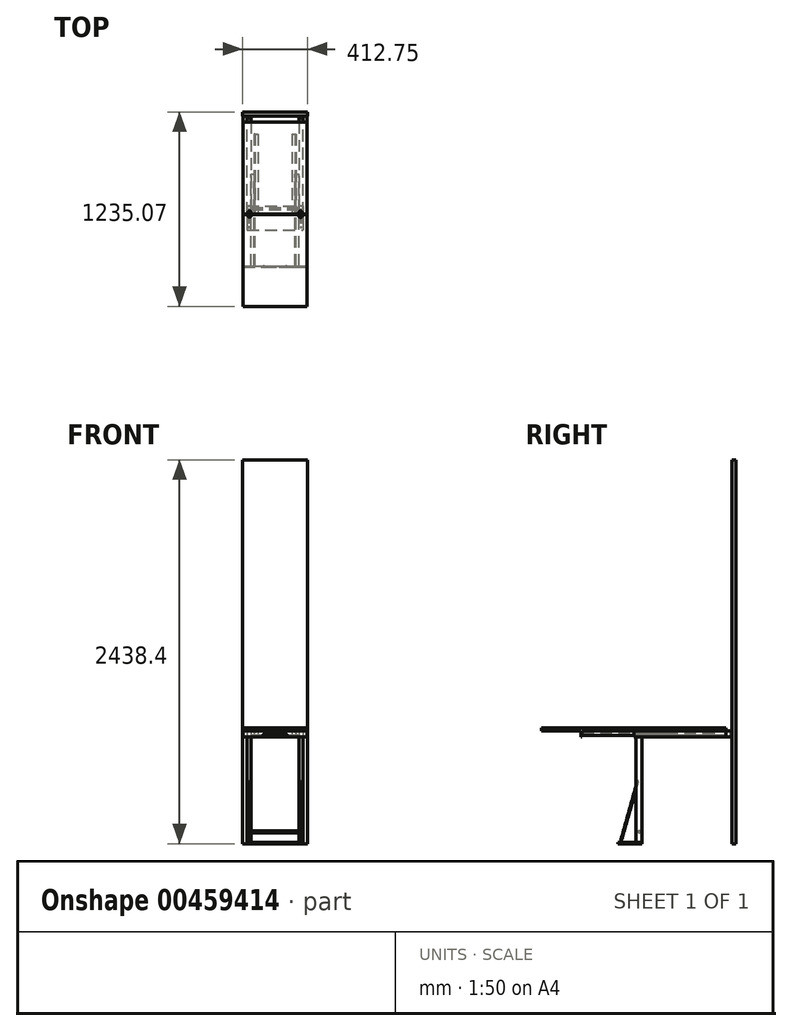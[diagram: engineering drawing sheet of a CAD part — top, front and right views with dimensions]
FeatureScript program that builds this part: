
annotation { "Feature Type Name" : "Feature", "Feature Type Description" : "" }
export const myFeature = defineFeature(function(context is Context, id is Id, definition is map)
    precondition{}
    {
        {
            var Q0;
            Q0=qCreatedBy(makeId("Front.planeOp"),FACE);
            var sketch = newSketch(context, id + "F0", { "sketchPlane" : qUnion([Q0])});
            skLineSegment(sketch, "E0.bottom", {"start": v(0, 0) * mm, "end": v(412.75, 0) * mm});
            skLineSegment(sketch, "E0.top", {"start": v(0, 2438.4) * mm, "end": v(412.75, 2438.4) * mm});
            skLineSegment(sketch, "E0.left", {"start": v(0, 0) * mm, "end": v(0, 2438.4) * mm});
            skLineSegment(sketch, "E0.right", {"start": v(412.75, 0) * mm, "end": v(412.75, 2438.4) * mm});
            skSolve(sketch);
        }
        {
            var Q0;
            Q0=qSketchRegion(id+"F0",true);
            extrude(context, id + "F1", {"entities" : qUnion([Q0]), "depth" : 25.4 * mm});
        }
        {
            var Q0;
            Q0=makeQuery(id+"F1.opExtrude","CAP_FACE",FACE,{"disambiguationData":[OSD([sQuery(id+"F0.wireOp",EDGE,"E0.bottom"),sQuery(id+"F0.wireOp",EDGE,"E0.top"),sQuery(id+"F0.wireOp",EDGE,"E0.left"),sQuery(id+"F0.wireOp",EDGE,"E0.right")])],"isStart":false});
            var sketch = newSketch(context, id + "F2", { "sketchPlane" : qUnion([Q0])});
            skLineSegment(sketch, "E1", {"start": v(206.38, 0) * mm, "end": v(206.38, 1295.4) * mm, "construction": true});
            skPoint(sketch, "E2", {"position": v(206.38, 736.6) * mm});
            skSolve(sketch);
        }
        {
            var Q0;
            Q0=makeQuery(id+"F2.imprint","IMPRINT",FACE,{"disambiguationData":[TD([[makeQuery(id+"F2.imprint","IMPRINT",EDGE,{"derivedFrom":makeQuery(id+"F1.opExtrude","CAP_EDGE",EDGE,{"disambiguationData":[OSD([sQuery(id+"F0.wireOp",EDGE,"E0.bottom")])],"isStart":false})}),1.0]])]});
            var sketch = newSketch(context, id + "F3", { "sketchPlane" : qUnion([Q0])});
            skLineSegment(sketch, "E3.bottom", {"start": v(3.17, 717.55) * mm, "end": v(409.58, 717.55) * mm});
            skLineSegment(sketch, "E3.top", {"start": v(3.18, 679.45) * mm, "end": v(409.57, 679.45) * mm});
            skLineSegment(sketch, "E3.left", {"start": v(3.17, 717.55) * mm, "end": v(3.17, 679.45) * mm});
            skLineSegment(sketch, "E3.right", {"start": v(409.57, 717.55) * mm, "end": v(409.57, 679.45) * mm});
            skLineSegment(sketch, "E4", {"start": v(206.37, 717.55) * mm, "end": v(206.37, 764.95) * mm, "construction": true});
            skSolve(sketch);
        }
        {
            var Q0;
            Q0 = qSketchRegion(id + "F3", true);
            extrude(context, id + "F4", {"entities" : qUnion([Q0]), "depth" : 38.1 * mm});
        }
        {
            var Q0;
            Q0=makeQuery(id+"F4.opExtrude","SWEPT_FACE",FACE,{"disambiguationData":[OSD([sQuery(id+"F3.wireOp",EDGE,"E3.bottom")])]});
            var sketch = newSketch(context, id + "F5", { "sketchPlane" : qUnion([Q0])});
            skLineSegment(sketch, "E5.bottom", {"start": v(3.17, -25.4) * mm, "end": v(409.58, -25.4) * mm});
            skLineSegment(sketch, "E5.top", {"start": v(3.17, -43.66) * mm, "end": v(409.58, -43.66) * mm});
            skLineSegment(sketch, "E5.left", {"start": v(3.17, -25.4) * mm, "end": v(3.17, -43.66) * mm});
            skLineSegment(sketch, "E5.right", {"start": v(409.58, -25.4) * mm, "end": v(409.58, -43.66) * mm});
            skLineSegment(sketch, "E6.bottom", {"start": v(3.17, -63.5) * mm, "end": v(409.58, -63.5) * mm});
            skLineSegment(sketch, "E6.top", {"start": v(3.17, -45.24) * mm, "end": v(409.58, -45.24) * mm});
            skLineSegment(sketch, "E6.left", {"start": v(3.17, -63.5) * mm, "end": v(3.17, -45.24) * mm});
            skLineSegment(sketch, "E6.right", {"start": v(409.58, -63.5) * mm, "end": v(409.58, -45.24) * mm});
            skSolve(sketch);
        }
        {
            var Q0;
            Q0 = qSketchRegion(id + "F5", true);
            var Q1;
            Q1=sQuery(id+"F2.wireOp",VERTEX,"E1.end");
            extrude(context, id + "F6", {"entities" : qUnion([Q0]), "endBound" : BoundingType.UP_TO_VERTEX, "endBoundEntityVertex" : qUnion([Q1]), "depth" : 25.4 * mm});
        }
        {
            var Q0;
            Q0=makeQuery(id+"F4.opExtrude","CAP_FACE",FACE,{"disambiguationData":[OSD([sQuery(id+"F3.wireOp",EDGE,"E3.bottom"),sQuery(id+"F3.wireOp",EDGE,"E3.top"),sQuery(id+"F3.wireOp",EDGE,"E3.left"),sQuery(id+"F3.wireOp",EDGE,"E3.right")])],"isStart":false});
            var sketch = newSketch(context, id + "F7", { "sketchPlane" : qUnion([Q0])});
            skLineSegment(sketch, "E7.bottom", {"start": v(3.17, 717.55) * mm, "end": v(28.57, 717.55) * mm});
            skLineSegment(sketch, "E7.top", {"start": v(3.17, 679.45) * mm, "end": v(28.57, 679.45) * mm});
            skLineSegment(sketch, "E7.left", {"start": v(3.17, 717.55) * mm, "end": v(3.17, 679.45) * mm});
            skLineSegment(sketch, "E7.right", {"start": v(28.57, 717.55) * mm, "end": v(28.57, 679.45) * mm});
            skLineSegment(sketch, "E8.bottom", {"start": v(409.57, 679.45) * mm, "end": v(384.17, 679.45) * mm});
            skLineSegment(sketch, "E8.top", {"start": v(409.57, 717.55) * mm, "end": v(384.17, 717.55) * mm});
            skLineSegment(sketch, "E8.left", {"start": v(409.57, 679.45) * mm, "end": v(409.57, 717.55) * mm});
            skLineSegment(sketch, "E8.right", {"start": v(384.17, 679.45) * mm, "end": v(384.17, 717.55) * mm});
            skSolve(sketch);
        }
        {
            var Q0;
            Q0 = qSketchRegion(id + "F7", true);
            extrude(context, id + "F8", {"entities" : qUnion([Q0]), "depth" : 584.2 * mm});
        }
        {
            var Q0;
            Q0=makeQuery(id+"F8.opExtrude","CAP_FACE",FACE,{"disambiguationData":[OSD([sQuery(id+"F7.wireOp",EDGE,"E8.bottom"),sQuery(id+"F7.wireOp",EDGE,"E8.top"),sQuery(id+"F7.wireOp",EDGE,"E8.left"),sQuery(id+"F7.wireOp",EDGE,"E8.right")])],"isStart":false});
            var sketch = newSketch(context, id + "F9", { "sketchPlane" : qUnion([Q0])});
            skLineSegment(sketch, "E9.bottom", {"start": v(53.97, 717.55) * mm, "end": v(79.37, 717.55) * mm});
            skLineSegment(sketch, "E9.top", {"start": v(53.97, 679.45) * mm, "end": v(79.37, 679.45) * mm});
            skLineSegment(sketch, "E9.left", {"start": v(53.97, 717.55) * mm, "end": v(53.97, 679.45) * mm});
            skLineSegment(sketch, "E9.right", {"start": v(79.37, 717.55) * mm, "end": v(79.37, 704.85) * mm});
            skLineSegment(sketch, "E10.bottom", {"start": v(333.38, 717.55) * mm, "end": v(358.78, 717.55) * mm});
            skLineSegment(sketch, "E10.top", {"start": v(333.38, 679.45) * mm, "end": v(358.78, 679.45) * mm});
            skLineSegment(sketch, "E10.left", {"start": v(333.38, 717.55) * mm, "end": v(333.38, 704.85) * mm});
            skLineSegment(sketch, "E10.right", {"start": v(358.78, 717.55) * mm, "end": v(358.78, 679.45) * mm});
            skLineSegment(sketch, "E11", {"start": v(53.97, 698.5) * mm, "end": v(358.78, 698.5) * mm, "construction": true});
            skLineSegment(sketch, "E12", {"start": v(358.78, 698.5) * mm, "end": v(206.37, 698.5) * mm, "construction": true});
            skLineSegment(sketch, "E13", {"start": v(206.37, 698.5) * mm, "end": v(206.37, 1295.4) * mm, "construction": true});
            skLineSegment(sketch, "E14.bottom", {"start": v(79.37, 704.85) * mm, "end": v(73.02, 704.85) * mm});
            skLineSegment(sketch, "E14.top", {"start": v(79.37, 692.15) * mm, "end": v(73.02, 692.15) * mm});
            skLineSegment(sketch, "E14.right", {"start": v(73.02, 704.85) * mm, "end": v(73.02, 692.15) * mm});
            skLineSegment(sketch, "E15.bottom", {"start": v(333.38, 704.85) * mm, "end": v(339.73, 704.85) * mm});
            skLineSegment(sketch, "E15.top", {"start": v(333.38, 692.15) * mm, "end": v(339.73, 692.15) * mm});
            skLineSegment(sketch, "E15.right", {"start": v(339.73, 704.85) * mm, "end": v(339.73, 692.15) * mm});
            skLineSegment(sketch, "E16", {"start": v(73.02, 698.5) * mm, "end": v(91.35, 698.5) * mm, "construction": true});
            skLineSegment(sketch, "E17.trimOffspring", {"start": v(79.37, 692.15) * mm, "end": v(79.37, 679.45) * mm});
            skLineSegment(sketch, "E18.trimOffspring", {"start": v(333.38, 692.15) * mm, "end": v(333.38, 679.45) * mm});
            skSolve(sketch);
        }
        {
            var Q0;
            Q0 = qSketchRegion(id + "F9", true);
            extrude(context, id + "F10", {"entities" : qUnion([Q0]), "depth" : 330.2 * mm, "hasSecondDirection" : true, "secondDirectionOppositeDirection" : true, "secondDirectionDepth" : 254 * mm});
        }
        {
            var Q0;
            Q0=makeQuery(id+"F10.opExtrude","CAP_FACE",FACE,{"disambiguationData":[OSD([sQuery(id+"F9.wireOp",EDGE,"E9.bottom"),sQuery(id+"F9.wireOp",EDGE,"E9.top"),sQuery(id+"F9.wireOp",EDGE,"E9.left"),sQuery(id+"F9.wireOp",EDGE,"E9.right"),sQuery(id+"F9.wireOp",EDGE,"E14.bottom"),sQuery(id+"F9.wireOp",EDGE,"E14.top"),sQuery(id+"F9.wireOp",EDGE,"E14.right"),sQuery(id+"F9.wireOp",EDGE,"E17.trimOffspring")])],"isStart":false});
            var sketch = newSketch(context, id + "F11", { "sketchPlane" : qUnion([Q0])});
            skLineSegment(sketch, "E19.bottom", {"start": v(53.97, 679.45) * mm, "end": v(358.78, 679.45) * mm});
            skLineSegment(sketch, "E19.top", {"start": v(53.97, 717.55) * mm, "end": v(358.78, 717.55) * mm});
            skLineSegment(sketch, "E19.left", {"start": v(53.97, 679.45) * mm, "end": v(53.97, 717.55) * mm});
            skLineSegment(sketch, "E19.right", {"start": v(358.78, 679.45) * mm, "end": v(358.78, 717.55) * mm});
            skSolve(sketch);
        }
        {
            var Q0;
            Q0 = qSketchRegion(id + "F11", true);
            extrude(context, id + "F12", {"entities" : qUnion([Q0]), "depth" : 6.35 * mm});
        }
        {
            var Q0;
            Q0=makeQuery(id+"F8.opExtrude","CAP_FACE",FACE,{"disambiguationData":[OSD([sQuery(id+"F7.wireOp",EDGE,"E7.bottom"),sQuery(id+"F7.wireOp",EDGE,"E7.top"),sQuery(id+"F7.wireOp",EDGE,"E7.left"),sQuery(id+"F7.wireOp",EDGE,"E7.right")])],"isStart":false});
            var sketch = newSketch(context, id + "F13", { "sketchPlane" : qUnion([Q0])});
            skLineSegment(sketch, "E20.0", {"start": v(79.37, 717.55) * mm, "end": v(79.37, 704.85) * mm});
            skLineSegment(sketch, "E20.1", {"start": v(79.37, 704.85) * mm, "end": v(73.02, 704.85) * mm});
            skLineSegment(sketch, "E20.2", {"start": v(73.02, 704.85) * mm, "end": v(73.02, 692.15) * mm});
            skLineSegment(sketch, "E20.3", {"start": v(79.37, 692.15) * mm, "end": v(73.02, 692.15) * mm});
            skLineSegment(sketch, "E20.4", {"start": v(79.37, 692.15) * mm, "end": v(79.37, 679.45) * mm});
            skLineSegment(sketch, "E20.5", {"start": v(333.38, 717.55) * mm, "end": v(333.38, 704.85) * mm});
            skLineSegment(sketch, "E20.6", {"start": v(333.38, 704.85) * mm, "end": v(339.73, 704.85) * mm});
            skLineSegment(sketch, "E20.7", {"start": v(339.73, 704.85) * mm, "end": v(339.73, 692.15) * mm});
            skLineSegment(sketch, "E20.8", {"start": v(333.38, 692.15) * mm, "end": v(339.73, 692.15) * mm});
            skLineSegment(sketch, "E20.9", {"start": v(333.38, 692.15) * mm, "end": v(333.38, 679.45) * mm});
            skLineSegment(sketch, "E21", {"start": v(333.38, 717.55) * mm, "end": v(314.33, 717.55) * mm});
            skLineSegment(sketch, "E22", {"start": v(314.33, 717.55) * mm, "end": v(314.33, 679.45) * mm});
            skLineSegment(sketch, "E23", {"start": v(314.33, 679.45) * mm, "end": v(333.38, 679.45) * mm});
            skLineSegment(sketch, "E24", {"start": v(79.37, 717.55) * mm, "end": v(98.42, 717.55) * mm});
            skLineSegment(sketch, "E25", {"start": v(98.42, 717.55) * mm, "end": v(98.42, 679.45) * mm});
            skLineSegment(sketch, "E26", {"start": v(98.42, 679.45) * mm, "end": v(79.37, 679.45) * mm});
            skSolve(sketch);
        }
        {
            var Q0;
            Q0 = qSketchRegion(id + "F13", true);
            extrude(context, id + "F14", {"entities" : qUnion([Q0]), "oppositeDirection" : true, "depth" : 508 * mm});
        }
        {
            var Q0;
            Q0=makeQuery(id+"F14.opExtrude","SWEPT_FACE",FACE,{"disambiguationData":[OSD([sQuery(id+"F13.wireOp",EDGE,"E23")])]});
            var sketch = newSketch(context, id + "F15", { "sketchPlane" : qUnion([Q0])});
            skLineSegment(sketch, "E27.bottom", {"start": v(44.15, 977.9) * mm, "end": v(373.47, 977.9) * mm});
            skLineSegment(sketch, "E27.top", {"start": v(44.15, 63.5) * mm, "end": v(373.47, 63.5) * mm});
            skLineSegment(sketch, "E27.left", {"start": v(44.15, 977.9) * mm, "end": v(44.15, 63.5) * mm});
            skLineSegment(sketch, "E27.right", {"start": v(373.47, 977.9) * mm, "end": v(373.47, 63.5) * mm});
            skSolve(sketch);
        }
        {
            var Q0;
            Q0 = qSketchRegion(id + "F15", true);
            extrude(context, id + "F16", {"entities" : qUnion([Q0]), "operationType" : NewBodyOperationType.REMOVE, "oppositeDirection" : true, "depth" : 9.52 * mm});
        }
        {
            var Q0;
            Q0=makeQuery(id+"F8.opExtrude","SWEPT_FACE",FACE,{"disambiguationData":[OSD([sQuery(id+"F7.wireOp",EDGE,"E8.bottom")])]});
            var sketch = newSketch(context, id + "F17", { "sketchPlane" : qUnion([Q0])});
            skLineSegment(sketch, "E28.bottom", {"start": v(53.97, 647.7) * mm, "end": v(358.78, 647.7) * mm});
            skLineSegment(sketch, "E28.top", {"start": v(53.97, 63.5) * mm, "end": v(358.78, 63.5) * mm});
            skLineSegment(sketch, "E28.left", {"start": v(53.97, 647.7) * mm, "end": v(53.97, 63.5) * mm});
            skLineSegment(sketch, "E28.right", {"start": v(358.78, 647.7) * mm, "end": v(358.78, 63.5) * mm});
            skSolve(sketch);
        }
        {
            var Q0;
            Q0 = qSketchRegion(id + "F17", true);
            var Q1;
            {var subQ5=sQuery(id+"F9.wireOp",EDGE,"E9.left");Q1=makeQuery(id+"F16.boolean.opBoolean","COPY",FACE,{"disambiguationData":[TD([makeQuery(id+"F10.opExtrude","SWEPT_FACE",FACE,{"disambiguationData":[OSD([subQ5])]})])],"derivedFrom":makeQuery(id+"F16.opExtrude","CAP_FACE",FACE,{"disambiguationData":[OSD([sQuery(id+"F15.wireOp",EDGE,"E27.bottom"),sQuery(id+"F15.wireOp",EDGE,"E27.top"),sQuery(id+"F15.wireOp",EDGE,"E27.left"),sQuery(id+"F15.wireOp",EDGE,"E27.right")])],"isStart":false})});}
            extrude(context, id + "F18", {"entities" : qUnion([Q0]), "endBound" : BoundingType.UP_TO_SURFACE, "oppositeDirection" : true, "endBoundEntityFace" : qUnion([Q1]), "depth" : 25.4 * mm});
        }
        {
            var Q0;
            Q0=makeQuery(id+"F12.opExtrude","CAP_FACE",FACE,{"disambiguationData":[OSD([sQuery(id+"F11.wireOp",EDGE,"E19.bottom"),sQuery(id+"F11.wireOp",EDGE,"E19.top"),sQuery(id+"F11.wireOp",EDGE,"E19.left"),sQuery(id+"F11.wireOp",EDGE,"E19.right")])],"isStart":false});
            var sketch = newSketch(context, id + "F19", { "sketchPlane" : qUnion([Q0])});
            skLineSegment(sketch, "E29.top", {"start": v(139.7, 698.5) * mm, "end": v(273.05, 698.5) * mm});
            skLineSegment(sketch, "E29.left", {"start": v(130.17, 685.8) * mm, "end": v(130.17, 688.98) * mm});
            skLineSegment(sketch, "E29.right", {"start": v(282.57, 685.8) * mm, "end": v(282.57, 688.98) * mm});
            skLineSegment(sketch, "E30", {"start": v(206.37, 698.5) * mm, "end": v(206.37, 717.55) * mm, "construction": true});
            skPoint(sketch, "E31.visualSharp", {"position": v(130.17, 698.5) * mm});
            skArc(sketch, "E31.filletArc", {"start": v(139.7, 698.5) * mm, "mid": v(132.96, 695.71) * mm, "end": v(130.17, 688.98) * mm});
            skPoint(sketch, "E32.visualSharp", {"position": v(282.58, 698.5) * mm});
            skArc(sketch, "E32.filletArc", {"start": v(282.57, 688.98) * mm, "mid": v(279.79, 695.71) * mm, "end": v(273.05, 698.5) * mm});
            skLineSegment(sketch, "E33", {"start": v(123.82, 679.45) * mm, "end": v(104.54, 679.45) * mm});
            skLineSegment(sketch, "E34", {"start": v(104.54, 679.45) * mm, "end": v(95.15, 663.43) * mm});
            skLineSegment(sketch, "E35", {"start": v(95.15, 663.43) * mm, "end": v(306.09, 663.43) * mm});
            skLineSegment(sketch, "E36", {"start": v(306.09, 663.43) * mm, "end": v(306.09, 679.45) * mm});
            skLineSegment(sketch, "E37", {"start": v(306.09, 679.45) * mm, "end": v(288.92, 679.45) * mm});
            skPoint(sketch, "E38.visualSharp", {"position": v(130.17, 679.45) * mm});
            skArc(sketch, "E38.filletArc", {"start": v(123.82, 679.45) * mm, "mid": v(128.32, 681.3) * mm, "end": v(130.17, 685.8) * mm});
            skPoint(sketch, "E39.visualSharp", {"position": v(282.57, 679.45) * mm});
            skArc(sketch, "E39.filletArc", {"start": v(282.58, 685.8) * mm, "mid": v(284.43, 681.3) * mm, "end": v(288.92, 679.45) * mm});
            skSolve(sketch);
        }
        {
            var Q0;
            Q0 = qSketchRegion(id + "F19", true);
            extrude(context, id + "F20", {"entities" : qUnion([Q0]), "operationType" : NewBodyOperationType.REMOVE, "oppositeDirection" : true, "depth" : 25.4 * mm});
        }
        {
            var Q0;
            Q0=makeQuery(id+"F8.opExtrude","SWEPT_FACE",FACE,{"disambiguationData":[OSD([sQuery(id+"F7.wireOp",EDGE,"E7.bottom")])]});
            var sketch = newSketch(context, id + "F21", { "sketchPlane" : qUnion([Q0])});
            skLineSegment(sketch, "E40.bottom", {"start": v(3.17, -63.5) * mm, "end": v(409.58, -63.5) * mm});
            skLineSegment(sketch, "E40.top", {"start": v(3.17, -647.7) * mm, "end": v(409.58, -647.7) * mm});
            skLineSegment(sketch, "E40.left", {"start": v(3.17, -63.5) * mm, "end": v(3.17, -647.7) * mm});
            skLineSegment(sketch, "E40.right", {"start": v(409.58, -63.5) * mm, "end": v(409.58, -647.7) * mm});
            skLineSegment(sketch, "E41.bottom", {"start": v(3.17, -650.88) * mm, "end": v(409.58, -650.88) * mm});
            skLineSegment(sketch, "E41.top", {"start": v(3.17, -1235.08) * mm, "end": v(409.58, -1235.08) * mm});
            skLineSegment(sketch, "E41.left", {"start": v(3.17, -650.88) * mm, "end": v(3.17, -1235.08) * mm});
            skLineSegment(sketch, "E41.right", {"start": v(409.58, -650.88) * mm, "end": v(409.58, -1235.08) * mm});
            skSolve(sketch);
        }
        {
            var Q0;
            Q0 = qSketchRegion(id + "F21", true);
            extrude(context, id + "F22", {"entities" : qUnion([Q0]), "depth" : 19.05 * mm});
        }
        {
            var Q0;
            Q0=makeQuery(id+"F22.opExtrude","CAP_FACE",FACE,{"disambiguationData":[OSD([sQuery(id+"F21.wireOp",EDGE,"E40.bottom"),sQuery(id+"F21.wireOp",EDGE,"E40.top"),sQuery(id+"F21.wireOp",EDGE,"E40.left"),sQuery(id+"F21.wireOp",EDGE,"E40.right")])],"isStart":true});
            var sketch = newSketch(context, id + "F23", { "sketchPlane" : qUnion([Q0])});
            skLineSegment(sketch, "E42.bottom", {"start": v(28.57, 635) * mm, "end": v(53.97, 635) * mm});
            skLineSegment(sketch, "E42.top", {"start": v(28.57, 596.9) * mm, "end": v(53.97, 596.9) * mm});
            skLineSegment(sketch, "E42.left", {"start": v(28.57, 635) * mm, "end": v(28.57, 596.9) * mm});
            skLineSegment(sketch, "E42.right", {"start": v(53.97, 635) * mm, "end": v(53.97, 596.9) * mm});
            skLineSegment(sketch, "E43.bottom", {"start": v(358.78, 635) * mm, "end": v(384.17, 635) * mm});
            skLineSegment(sketch, "E43.top", {"start": v(358.78, 596.9) * mm, "end": v(384.17, 596.9) * mm});
            skLineSegment(sketch, "E43.left", {"start": v(358.78, 635) * mm, "end": v(358.78, 596.9) * mm});
            skLineSegment(sketch, "E43.right", {"start": v(384.17, 635) * mm, "end": v(384.17, 596.9) * mm});
            skSolve(sketch);
        }
        {
            var Q0;
            Q0 = qSketchRegion(id + "F23", true);
            var Q1;
            Q1=makeQuery(id+"F1.opExtrude","SWEPT_FACE",FACE,{"disambiguationData":[OSD([sQuery(id+"F0.wireOp",EDGE,"E0.bottom")])]});
            extrude(context, id + "F24", {"entities" : qUnion([Q0]), "endBound" : BoundingType.UP_TO_SURFACE, "endBoundEntityFace" : qUnion([Q1]), "depth" : 25.4 * mm});
        }
        {
            var Q0;
            Q0=makeQuery(id+"F24.opExtrude","CAP_FACE",FACE,{"disambiguationData":[OSD([sQuery(id+"F23.wireOp",EDGE,"E43.bottom"),sQuery(id+"F23.wireOp",EDGE,"E43.top"),sQuery(id+"F23.wireOp",EDGE,"E43.left"),sQuery(id+"F23.wireOp",EDGE,"E43.right")])],"isStart":false});
            var sketch = newSketch(context, id + "F25", { "sketchPlane" : qUnion([Q0])});
            skLineSegment(sketch, "E44.bottom", {"start": v(28.57, 596.9) * mm, "end": v(384.17, 596.9) * mm});
            skLineSegment(sketch, "E44.top", {"start": v(28.57, 749.3) * mm, "end": v(384.17, 749.3) * mm});
            skLineSegment(sketch, "E44.left", {"start": v(28.57, 596.9) * mm, "end": v(28.57, 749.3) * mm});
            skLineSegment(sketch, "E44.right", {"start": v(384.17, 596.9) * mm, "end": v(384.17, 749.3) * mm});
            skSolve(sketch);
        }
        {
            var Q0;
            Q0 = qSketchRegion(id + "F25", true);
            extrude(context, id + "F26", {"entities" : qUnion([Q0]), "oppositeDirection" : true, "depth" : 9.52 * mm});
        }
        {
            var Q0;
            Q0=makeQuery(id+"F4.opExtrude","SWEPT_FACE",FACE,{"disambiguationData":[OSD([sQuery(id+"F3.wireOp",EDGE,"E3.top")])]});
            var sketch = newSketch(context, id + "F27", { "sketchPlane" : qUnion([Q0])});
            skLineSegment(sketch, "E45.bottom", {"start": v(28.57, 63.5) * mm, "end": v(53.97, 63.5) * mm});
            skLineSegment(sketch, "E45.top", {"start": v(28.57, 38.1) * mm, "end": v(53.97, 38.1) * mm});
            skLineSegment(sketch, "E45.left", {"start": v(28.57, 63.5) * mm, "end": v(28.57, 38.1) * mm});
            skLineSegment(sketch, "E45.right", {"start": v(53.97, 63.5) * mm, "end": v(53.97, 38.1) * mm});
            skLineSegment(sketch, "E46.bottom", {"start": v(358.78, 63.5) * mm, "end": v(384.18, 63.5) * mm});
            skLineSegment(sketch, "E46.top", {"start": v(358.78, 38.1) * mm, "end": v(384.18, 38.1) * mm});
            skLineSegment(sketch, "E46.left", {"start": v(358.78, 63.5) * mm, "end": v(358.78, 38.1) * mm});
            skLineSegment(sketch, "E46.right", {"start": v(384.18, 63.5) * mm, "end": v(384.18, 38.1) * mm});
            skSolve(sketch);
        }
        {
            var Q0;
            Q0 = qSketchRegion(id + "F27", true);
            var Q1;
            Q1=makeQuery(id+"F4.opExtrude","SWEPT_FACE",FACE,{"disambiguationData":[OSD([sQuery(id+"F3.wireOp",EDGE,"E3.bottom")])]});
            extrude(context, id + "F28", {"entities" : qUnion([Q0]), "operationType" : NewBodyOperationType.REMOVE, "endBound" : BoundingType.UP_TO_SURFACE, "oppositeDirection" : true, "endBoundEntityFace" : qUnion([Q1]), "depth" : 25.4 * mm});
        }
        {
            var Q0;
            Q0=makeQuery(id+"F24.opExtrude","SWEPT_FACE",FACE,{"disambiguationData":[OSD([sQuery(id+"F23.wireOp",EDGE,"E42.bottom")])]});
            var sketch = newSketch(context, id + "F29", { "sketchPlane" : qUnion([Q0])});
            skLineSegment(sketch, "E47", {"start": v(28.57, 358.78) * mm, "end": v(53.97, 358.78) * mm, "construction": true});
            skLineSegment(sketch, "E48", {"start": v(41.27, 358.78) * mm, "end": v(41.27, 12.63) * mm, "construction": true});
            skLineSegment(sketch, "E49", {"start": v(358.78, 358.78) * mm, "end": v(384.17, 358.78) * mm, "construction": true});
            skLineSegment(sketch, "E50", {"start": v(371.48, 358.78) * mm, "end": v(371.48, 99.9) * mm, "construction": true});
            skSolve(sketch);
        }
        {
            var Q0;
            Q0=makeQuery(id+"F1.opExtrude","SWEPT_FACE",FACE,{"disambiguationData":[OSD([sQuery(id+"F0.wireOp",EDGE,"E0.left")])]});
            var Q1;
            Q1=sQuery(id+"F29.wireOp",EDGE,"E48");
            cPlane(context, id + "F30", {"entities" : qUnion([Q0, Q1]), "cplaneType" : CPlaneType.LINE_ANGLE, "offset" : 25.4 * mm, "angle" : 0 * degree, "width" : 152.4 * mm, "height" : 152.4 * mm});
        }
        {
            var Q0;
            Q0=sQuery(id+"F29.wireOp",EDGE,"E50");
            var Q1;
            Q1=makeQuery(id+"F1.opExtrude","SWEPT_FACE",FACE,{"disambiguationData":[OSD([sQuery(id+"F0.wireOp",EDGE,"E0.left")])]});
            cPlane(context, id + "F31", {"entities" : qUnion([Q0, Q1]), "cplaneType" : CPlaneType.LINE_ANGLE, "offset" : 25.4 * mm, "angle" : 0 * degree, "width" : 152.4 * mm, "height" : 152.4 * mm});
        }
        {
            var Q0;
            Q0=qCreatedBy(id+"F30.planeOp",FACE);
            var sketch = newSketch(context, id + "F32", { "sketchPlane" : qUnion([Q0])});
            skLineSegment(sketch, "E51", {"start": v(-635.27, 358.16) * mm, "end": v(-733.4, 9.53) * mm});
            skLineSegment(sketch, "E52", {"start": v(-635.27, 358.16) * mm, "end": v(-623.6, 399.62) * mm});
            skSolve(sketch);
        }
        {
            var Q0;
            Q0=qCreatedBy(id+"F31.planeOp",FACE);
            var sketch = newSketch(context, id + "F33", { "sketchPlane" : qUnion([Q0])});
            skLineSegment(sketch, "E53.0", {"start": v(-635.27, 358.16) * mm, "end": v(-733.4, 9.53) * mm});
            skSolve(sketch);
        }
        {
            var Q0;
            Q0=makeQuery(id+"F26.opExtrude","CAP_FACE",FACE,{"disambiguationData":[OSD([sQuery(id+"F25.wireOp",EDGE,"E44.bottom"),sQuery(id+"F25.wireOp",EDGE,"E44.top"),sQuery(id+"F25.wireOp",EDGE,"E44.left"),sQuery(id+"F25.wireOp",EDGE,"E44.right")])],"isStart":false});
            var sketch = newSketch(context, id + "F34", { "sketchPlane" : qUnion([Q0])});
            skCircle(sketch, "E54", {"center": v(41.27, -733.4) * mm, "radius": 2.54 * mm});
            skCircle(sketch, "E55", {"center": v(371.48, -733.4) * mm, "radius": 2.54 * mm});
            skSolve(sketch);
        }
        {
            var Q0;
            Q0=makeQuery(id+"F34.imprint","IMPRINT",FACE,{"disambiguationData":[TD([[makeQuery(id+"F34.imprint","IMPRINT",EDGE,{"derivedFrom":sQuery(id+"F34.wireOp",EDGE,"E54")}),1.0]])]});
            var Q1;
            Q1=makeQuery(id+"F34.imprint","IMPRINT",FACE,{"disambiguationData":[TD([[makeQuery(id+"F34.imprint","IMPRINT",EDGE,{"derivedFrom":sQuery(id+"F34.wireOp",EDGE,"E55")}),1.0]])]});
            var Q2;
            Q2=sQuery(id+"F32.wireOp",EDGE,"E51");
            var Q3;
            Q3=sQuery(id+"F32.wireOp",EDGE,"E52");
            sweep(context, id + "F35", {"profiles" : qUnion([Q0, Q1]), "path" : qUnion([Q2, Q3]), "keepProfileOrientation" : true});
        }
        {
            var Q0;
            Q0=makeQuery(id+"F24.opExtrude","SWEPT_FACE",FACE,{"disambiguationData":[OSD([sQuery(id+"F23.wireOp",EDGE,"E42.right")])]});
            var sketch = newSketch(context, id + "F36", { "sketchPlane" : qUnion([Q0])});
            skCircle(sketch, "E56", {"center": v(-615.95, 76.2) * mm, "radius": 6.35 * mm});
            skLineSegment(sketch, "E57", {"start": v(-615.95, 76.2) * mm, "end": v(-615.95, 0) * mm, "construction": true});
            skSolve(sketch);
        }
        {
            var Q0;
            Q0 = qSketchRegion(id + "F36", true);
            extrude(context, id + "F37", {"entities" : qUnion([Q0]), "endBound" : BoundingType.UP_TO_NEXT, "depth" : 25.4 * mm});
        }
        {
            var Q0;
            Q0=makeQuery(id+"F6.opExtrude","SWEPT_BODY",BODY,{"disambiguationData":[OSD([sQuery(id+"F5.wireOp",EDGE,"E5.bottom"),sQuery(id+"F5.wireOp",EDGE,"E5.top"),sQuery(id+"F5.wireOp",EDGE,"E5.left"),sQuery(id+"F5.wireOp",EDGE,"E5.right")])]});
            var Q1;
            Q1=makeQuery(id+"F6.opExtrude","SWEPT_BODY",BODY,{"disambiguationData":[OSD([sQuery(id+"F5.wireOp",EDGE,"E6.bottom"),sQuery(id+"F5.wireOp",EDGE,"E6.top"),sQuery(id+"F5.wireOp",EDGE,"E6.left"),sQuery(id+"F5.wireOp",EDGE,"E6.right")])]});
            deleteBodies(context, id + "F38", {"entities" : qUnion([Q0, Q1])});
        }
        {
            var Q0;
            Q0=makeQuery(id+"F12.opExtrude","CAP_FACE",FACE,{"disambiguationData":[OSD([sQuery(id+"F11.wireOp",EDGE,"E19.bottom"),sQuery(id+"F11.wireOp",EDGE,"E19.top"),sQuery(id+"F11.wireOp",EDGE,"E19.left"),sQuery(id+"F11.wireOp",EDGE,"E19.right")])],"isStart":false});
            var sketch = newSketch(context, id + "F39", { "sketchPlane" : qUnion([Q0])});
            skLineSegment(sketch, "E58.bottom", {"start": v(358.78, 679.45) * mm, "end": v(409.58, 679.45) * mm});
            skLineSegment(sketch, "E58.top", {"start": v(358.78, 717.55) * mm, "end": v(409.58, 717.55) * mm});
            skLineSegment(sketch, "E58.left", {"start": v(358.78, 679.45) * mm, "end": v(358.78, 717.55) * mm});
            skLineSegment(sketch, "E58.right", {"start": v(409.58, 679.45) * mm, "end": v(409.58, 717.55) * mm});
            skLineSegment(sketch, "E59.bottom", {"start": v(53.97, 679.45) * mm, "end": v(3.17, 679.45) * mm});
            skLineSegment(sketch, "E59.top", {"start": v(53.97, 717.55) * mm, "end": v(3.17, 717.55) * mm});
            skLineSegment(sketch, "E59.left", {"start": v(53.97, 679.45) * mm, "end": v(53.97, 717.55) * mm});
            skLineSegment(sketch, "E59.right", {"start": v(3.17, 679.45) * mm, "end": v(3.17, 717.55) * mm});
            skSolve(sketch);
        }
        {
            var Q0;
            Q0 = qSketchRegion(id + "F39", true);
            extrude(context, id + "F40", {"entities" : qUnion([Q0]), "operationType" : NewBodyOperationType.ADD, "oppositeDirection" : true, "depth" : 6.35 * mm});
        }
        {
            var Q0;
            Q0=makeQuery(id+"F22.opExtrude","CAP_FACE",FACE,{"disambiguationData":[OSD([sQuery(id+"F21.wireOp",EDGE,"E40.bottom"),sQuery(id+"F21.wireOp",EDGE,"E40.top"),sQuery(id+"F21.wireOp",EDGE,"E40.left"),sQuery(id+"F21.wireOp",EDGE,"E40.right")])],"isStart":false});
            var sketch = newSketch(context, id + "F41", { "sketchPlane" : qUnion([Q0])});
            skLineSegment(sketch, "E60.bottom", {"start": v(41.27, -630.24) * mm, "end": v(47.63, -630.24) * mm});
            skLineSegment(sketch, "E60.top", {"start": v(41.27, -668.34) * mm, "end": v(47.63, -668.34) * mm});
            skLineSegment(sketch, "E60.left", {"start": v(34.92, -636.59) * mm, "end": v(34.92, -661.99) * mm});
            skLineSegment(sketch, "E60.right", {"start": v(53.97, -636.59) * mm, "end": v(53.97, -661.99) * mm});
            skLineSegment(sketch, "E61.bottom", {"start": v(365.12, -630.24) * mm, "end": v(371.48, -630.24) * mm});
            skLineSegment(sketch, "E61.top", {"start": v(365.12, -669.95) * mm, "end": v(371.48, -669.95) * mm});
            skLineSegment(sketch, "E61.left", {"start": v(358.77, -636.59) * mm, "end": v(358.77, -663.6) * mm});
            skLineSegment(sketch, "E61.right", {"start": v(377.83, -636.59) * mm, "end": v(377.83, -663.6) * mm});
            skLineSegment(sketch, "E62", {"start": v(53.97, -649.29) * mm, "end": v(358.77, -649.29) * mm, "construction": true});
            skPoint(sketch, "E62.endSnap0", {"position": v(358.78, -650.1) * mm});
            skLineSegment(sketch, "E63", {"start": v(206.37, -649.29) * mm, "end": v(206.37, -63.5) * mm, "construction": true});
            skPoint(sketch, "E64.visualSharp", {"position": v(34.92, -630.24) * mm});
            skArc(sketch, "E64.filletArc", {"start": v(41.27, -630.24) * mm, "mid": v(36.78, -632.1) * mm, "end": v(34.93, -636.59) * mm});
            skPoint(sketch, "E65.visualSharp", {"position": v(34.92, -668.34) * mm});
            skArc(sketch, "E65.filletArc", {"start": v(34.93, -661.99) * mm, "mid": v(36.78, -666.48) * mm, "end": v(41.27, -668.34) * mm});
            skPoint(sketch, "E66.visualSharp", {"position": v(53.97, -668.34) * mm});
            skArc(sketch, "E66.filletArc", {"start": v(47.63, -668.34) * mm, "mid": v(52.12, -666.48) * mm, "end": v(53.97, -661.99) * mm});
            skPoint(sketch, "E67.visualSharp", {"position": v(358.77, -630.24) * mm});
            skArc(sketch, "E67.filletArc", {"start": v(365.12, -630.24) * mm, "mid": v(360.63, -632.1) * mm, "end": v(358.78, -636.59) * mm});
            skPoint(sketch, "E68.visualSharp", {"position": v(377.83, -630.24) * mm});
            skArc(sketch, "E68.filletArc", {"start": v(377.83, -636.59) * mm, "mid": v(375.97, -632.1) * mm, "end": v(371.48, -630.24) * mm});
            skPoint(sketch, "E69.visualSharp", {"position": v(377.83, -669.95) * mm});
            skArc(sketch, "E69.filletArc", {"start": v(371.48, -669.95) * mm, "mid": v(375.97, -668.09) * mm, "end": v(377.83, -663.6) * mm});
            skPoint(sketch, "E70.visualSharp", {"position": v(358.77, -669.95) * mm});
            skArc(sketch, "E70.filletArc", {"start": v(358.77, -663.6) * mm, "mid": v(360.63, -668.09) * mm, "end": v(365.12, -669.95) * mm});
            skPoint(sketch, "E71.visualSharp", {"position": v(53.97, -630.24) * mm});
            skArc(sketch, "E71.filletArc", {"start": v(53.98, -636.59) * mm, "mid": v(52.12, -632.1) * mm, "end": v(47.63, -630.24) * mm});
            skSolve(sketch);
        }
        {
            var Q0;
            Q0 = qSketchRegion(id + "F41", true);
            extrude(context, id + "F42", {"entities" : qUnion([Q0]), "depth" : 0.25 * mm});
        }
    });
